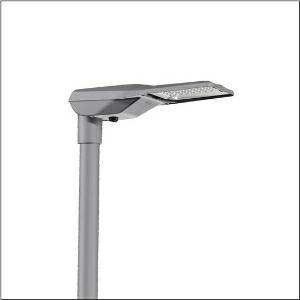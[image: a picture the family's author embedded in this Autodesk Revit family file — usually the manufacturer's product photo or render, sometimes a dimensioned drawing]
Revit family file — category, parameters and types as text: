
# Revit family: streetlight_sl_21_mini___p0_8a_5xe2u33r08jb_f297
name_source: partatom
category: Lighting Fixtures
units: mm (PartAtom-declared; Revit-internal decimal feet)

## family parameters
Cut with Voids When Loaded = No
Host = Face
Light Source = No
Part Type = Normal
Room Calculation Point = No
Round Connector Dimension = Use Diameter
Shared = No

## types (1)
- --- (1 x LED, 13050 lm, 88.6 W, 3000K)
    Apparent Load = 89 VA
    CIE Flux Codes = 36 69 97 100 100
    Color Rendering = 70
    Color Temperature = 3000K
    Default Elevation = 1800 mm
    Description = Streetlight SL 21 mini, mast luminaire, primary light control with lens, of PMMA, primary optical cover: cover, of toughened safety glass, transparent, light distribution: P0.8a, light emission: direct distribution, primary light characteristic: asymmetric, installation type: post-top, side-entry, LED, High Power LED, rated luminous flux: 13.050lm, luminous efficacy: 147lm/W, light colour: 730, colour temperature: 3000K, control gear: D4i, control: pre-setting: logarithmic dimming characteristic, flexible luminous flux parameterisation, time-dependent luminous flux control, constant luminous flux control, overheat protection, mains connection: 220..240V, AC, 50/60Hz, start of lifetime: 89W, end of service life: 92W, reduction: 41W, luminaire housing, of diecast aluminium, powder-coated, Siteco® metallic grey (DB 702S), corrosivity category C5 mid according to DIN EN ISO 12944, multi-level sealing system, sealing non-destructively replaceable, inclination adjustable: 0°, 5°, 10°, 15°, please order mast flange separately, length: 628mm, width: 235mm, height: 110mm, mast flange for spigot size: 42mm (side-entry): 5XC10008XM4, 60/48mm (side-entry/post-top): 5XC10108XM2, 76/60mm (side-entry/post-top): 5XC10108XM1, mounting height: 4..8m, Smart Interface below, protection rating (complete): IP66, insulation class (complete): insulation class II (safety insulation), certification: CE, ENEC, ENEC+, VDE, impact resistance: IK10, permissible operating ambient temperature for outdoor applications: -40..+50°C, standard-compliant lighting for roads and squares, packaging unit: 1 piece

Light Distribution: P0.8a
    Height = 110 mm
    Lamp = 1 x LED
    Lamp Light Flux = 13050 lm
    Lamp Power = 88.6 W
    Lamp count = 1
    Length = 625 mm
    Luminous efficacy = 147 lm/W
    Manufacturer = Siteco
    ModVariant = No
    Model = 5XE2U33R08JB
    Number of Poles = 1
    OnlyDefault = Yes
    Power Factor = 1
    Product Name = Streetlight SL 21 mini | P0.8a
    Product group = mast luminaire | pylon top
    ProductGroupID = 6100
    Protection Class = Protection class II
    Protection Degree = IP 66
    RLX_Detail_Level = 1
    RLX_Emergency_Light_Flux = 0 lm
    RLX_Emergency_Type = 0
    RLX_Emergency_Type_DB = No
    RlxData = <blob elided: 26201 chars, md5=ff46098a>
    Socket = socket
    Standby Power = 0 W
    System Light Flux = 13050 lm
    System Power = 89 W
    Type Comments = factory setting: luminous flux: 100 % | dim-lin: 254 | 915 mA
    Type Image = l_1003516.jpg
    URL = http://relux.com
    VarID = @adj_013357
    Voltage = 0 V
    Weight = 0.00 kg
    Width = 234 mm

## geometry (parser evidence)
native form markers: Blend x4, Sweep x8
no freeform markers — native parametric forms only
